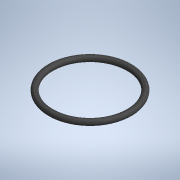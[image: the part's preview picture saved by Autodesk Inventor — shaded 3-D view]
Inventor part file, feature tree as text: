
AUTODESK INVENTOR PART (.ipt)
format: ipt  version: 2022 (Build 260153000, 153)  size: 103,936 bytes
history: mixed  units: mm (DEFAULTED — no unit token found)
features: other x8, revolve x1, imported_body x1
bodies: Body1 (imported_parasolid)
feature tree (10):
  other  "Sólido1"
  other  "Origen"
  other  "Plano YZ"
  other  "Plano XZ"
  other  "Plano XY"
  other  "Eje X"
  other  "Eje Y"
  other  "Eje Z"
  revolve  "Revolución1"  [1 undecoded]
  imported_body  NMx_Import_Brep_tag  [imported B-rep: ~1 faces, bbox_mm=None]
note: 1 required parameter value undecoded (feature->parameter linkage not recoverable at this tier; creation-order binding heuristic only, values carry confidence <= 0.55)
